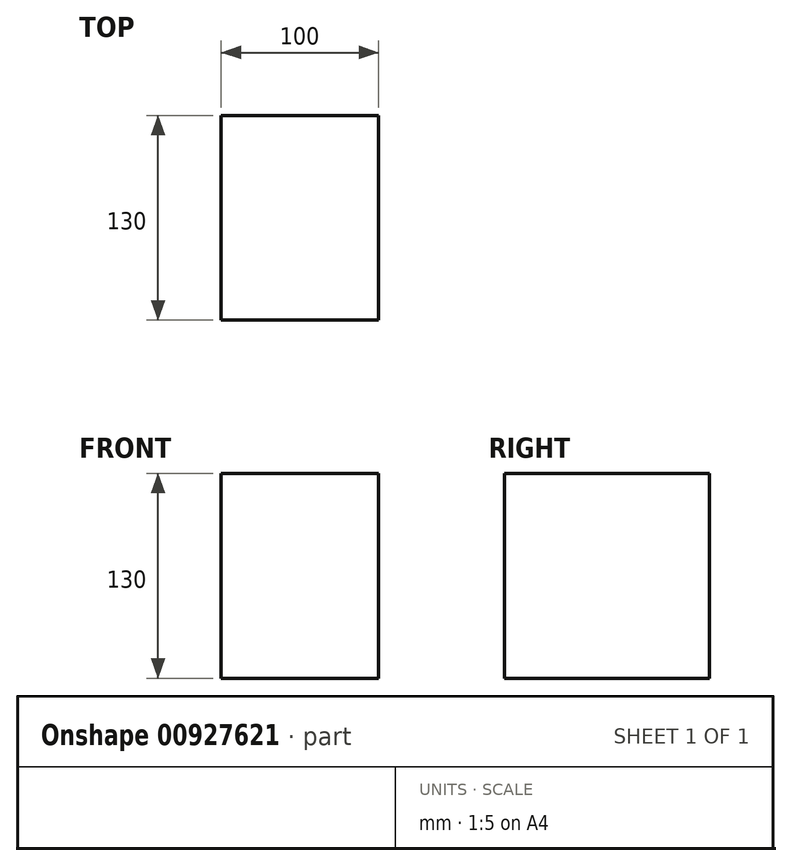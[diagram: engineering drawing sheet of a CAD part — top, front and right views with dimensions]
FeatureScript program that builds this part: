
annotation { "Feature Type Name" : "Feature", "Feature Type Description" : "" }
export const myFeature = defineFeature(function(context is Context, id is Id, definition is map)
    precondition{}
    {
        {
            var Q0;
            Q0=qCreatedBy(makeId("Right.planeOp"),FACE);
            var sketch = newSketch(context, id + "F0", { "sketchPlane" : qUnion([Q0])});
            skLineSegment(sketch, "E0.bottom", {"start": v(-65, 65) * mm, "end": v(65, 65) * mm});
            skLineSegment(sketch, "E0.top", {"start": v(-65, -65) * mm, "end": v(65, -65) * mm});
            skLineSegment(sketch, "E0.left", {"start": v(-65, 65) * mm, "end": v(-65, -65) * mm});
            skLineSegment(sketch, "E0.right", {"start": v(65, 65) * mm, "end": v(65, -65) * mm});
            skLineSegment(sketch, "E1", {"start": v(-65, -65) * mm, "end": v(65, 65) * mm, "construction": true});
            skSolve(sketch);
        }
        {
            var Q0;
            Q0=makeQuery(id+"F0.imprint","IMPRINT",FACE,{"disambiguationData":[TD([[makeQuery(id+"F0.imprint","IMPRINT",EDGE,{"derivedFrom":sQuery(id+"F0.wireOp",EDGE,"E0.bottom")}),-1.0]])]});
            extrude(context, id + "F1", {"entities" : qUnion([Q0]), "oppositeDirection" : true, "depth" : 100 * mm, "offsetDistance" : 25 * mm});
        }
    });
